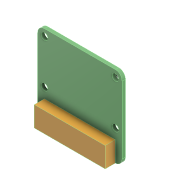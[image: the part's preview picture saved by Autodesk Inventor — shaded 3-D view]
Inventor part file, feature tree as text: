
AUTODESK INVENTOR PART (.ipt)
format: ipt  version: 2022 (Build 260153000, 153)  size: 186,880 bytes
history: native  units: mm
features: extrude x6, sketch x6, fillet x1
ambient origin geometry x8: Origin, YZ Plane, XZ Plane, XY Plane, X Axis, Y Axis, Z Axis, Center Point
bodies: Solid1 (feature_tree)
feature tree (13):
  extrude  "Extrusion1"  Depth=25.0mm
  extrude  "Extrusion2"  Depth=11.0mm
  extrude  "Extrusion3"  Depth=4.5mm
  extrude  "Extrusion4"  Depth=9.0mm
  extrude  "Extrusion5"  Depth=8.5mm
  extrude  "Extrusion6"  Depth=2.0mm
  fillet  "Fillet1"  Radius=7.0mm
  sketch  "Sketch1"  dims[d0=24.0mm d1=25.0mm]
  sketch  "Sketch2"  dims[d2=1.0mm d3=0.0mm d4=11.0mm]
  sketch  "Sketch3"  dims[d5=11.0mm d6=4.5mm]
  sketch  "Sketch4"  dims[d7=5.0mm d8=0.0mm d9=9.0mm]
  sketch  "Sketch5"  dims[d10=8.0mm d11=0.0mm d12=8.5mm]
  sketch  "Sketch6"  dims[d13=4.0mm d14=2.0mm d15=7.0mm d16=1.5mm d17=0.0mm d19=15.0mm d20=1.0mm d21=1.0mm d22=2.0mm d23=2.0mm d24=2.0mm d25=2.0mm d26=0.0mm d27=0.0mm d28=21.0mm d29=6.0mm d30=4.0mm d31=0.0mm d32=2.0mm]
